# Revit family: Astro Lighting - Can 50 Round
name_source: partatom
category: Lighting Fixtures
revit_build: Autodesk Revit 2018 (Build: 20170223_1515(x64)
units: mm (PartAtom-declared; Revit-internal decimal feet)

## family parameters
Always vertical = Yes
Cut with Voids When Loaded = No
Host = Ceiling
Light Source = No
OmniClass Number = 23.80.70.11
OmniClass Title = Luminaries for Internal Lighting
Part Type = Normal
Room Calculation Point = No
Round Connector Dimension = Use Diameter
Shared = No

## types (1)
- Astro Lighting - Can 50 Triple Round
    ADA compliant = Not Applicable
    Apparent Load = 0 VA
    Base = Astro Lighting - White
    Base Screw = Astro Lighting - Black
    Can Housing = Astro Lighting - White
    Can Joint = Astro Lighting - White
    Can Lens = Astro Lighting - Lens Cover
    Can Rear Cover = Astro Lighting - Black
    Can Reflective Cone = Astro Lighting - Reflective Cone
    Dimmable = Yes
    Dimming Method = Phase - Leading Edge & Trailing Edge
    Driver Included = Yes (Integral)
    Driver Required = Not Applicable
    Efficacy (lm/w) = 63.5lm/W
    Electrical Class = 1
    Lamp = LED Module
    Length of Cable Supplied = Not Applicable
    Light Source Fixed = Rotation Adjustment 0-330° & Tilt Adjustment 0-90° on all 3 Cans
    Location Rating = IP20
    Manufacturer = Astro Lighting Ltd
    Power (Watts) = 22.6
    Product Code = 6166
    Product Location = Indoor
    Product Name = Can 50 Triple Round
    Product SKU = 1396006
    URL = www.astrolighting.com
    Wattage Comments = Not Applicable

## geometry (parser evidence)
native form markers: Sweep x21
no freeform markers — native parametric forms only
